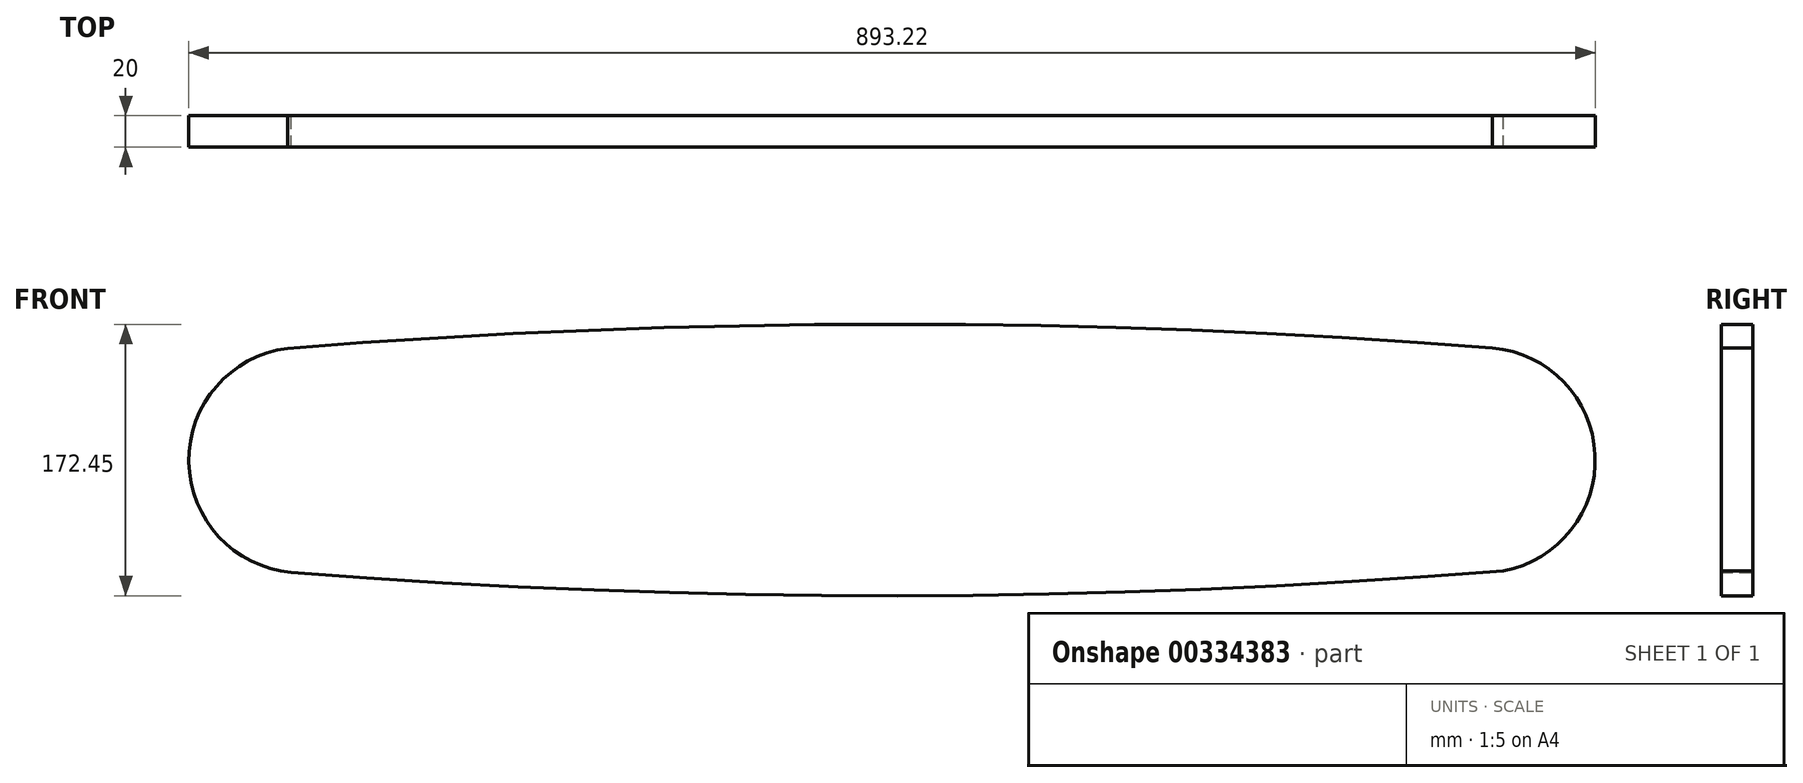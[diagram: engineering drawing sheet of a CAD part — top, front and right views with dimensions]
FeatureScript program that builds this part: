
annotation { "Feature Type Name" : "Feature", "Feature Type Description" : "" }
export const myFeature = defineFeature(function(context is Context, id is Id, definition is map)
    precondition{}
    {
        {
            var Q0;
            Q0=qCreatedBy(makeId("Front.planeOp"),FACE);
            var sketch = newSketch(context, id + "F0", { "sketchPlane" : qUnion([Q0])});
            skCircle(sketch, "E0", {"center": v(-63.48, 0) * mm, "radius": 71.61 * mm});
            skCircle(sketch, "E1", {"center": v(686.52, 0) * mm, "radius": 71.61 * mm});
            skLineSegment(sketch, "E2", {"start": v(686.52, 0) * mm, "end": v(-63.48, 0) * mm});
            skArc(sketch, "E3", {"start": v(-70.15, -71.3) * mm, "mid": v(314.9, -86.13) * mm, "end": v(699.91, -70.35) * mm});
            skArc(sketch, "E4", {"start": v(693, 71.32) * mm, "mid": v(310.28, 86.3) * mm, "end": v(-72.44, 71.05) * mm});
            skSolve(sketch);
        }
        {
            var Q0;
            {var subQ1=sQuery(id+"F0.wireOp",EDGE,"E0");var subQ4=sQuery(id+"F0.wireOp",EDGE,"E4");var subQ5=makeQuery(id+"F0.imprint","INTERSECT",VERTEX,{"disambiguationData":[OD(1.0)],"derivedFrom":[subQ1,subQ4]});Q0=makeQuery(id+"F0.imprint","IMPRINT",FACE,{"disambiguationData":[TD([[makeQuery(id+"F0.imprint","IMPRINT",EDGE,{"disambiguationData":[TD([[subQ5,1.0]])],"derivedFrom":subQ1}),1.0]])]});}
            var Q1;
            {var subQ0=sQuery(id+"F0.wireOp",EDGE,"E4");var subQ1=sQuery(id+"F0.wireOp",EDGE,"E0");var subQ2=makeQuery(id+"F0.imprint","INTERSECT",VERTEX,{"disambiguationData":[OD(1.0)],"derivedFrom":[subQ1,subQ0]});Q1=makeQuery(id+"F0.imprint","IMPRINT",FACE,{"disambiguationData":[TD([[makeQuery(id+"F0.imprint","IMPRINT",EDGE,{"disambiguationData":[TD([[subQ2,1.0]])],"derivedFrom":subQ1}),-1.0]])]});}
            var Q2;
            {var subQ0=sQuery(id+"F0.wireOp",EDGE,"E2");var subQ1=sQuery(id+"F0.wireOp",EDGE,"E0");var subQ2=makeQuery(id+"F0.imprint","INTERSECT",VERTEX,{"derivedFrom":[subQ1,subQ0]});Q2=makeQuery(id+"F0.imprint","IMPRINT",FACE,{"disambiguationData":[TD([[makeQuery(id+"F0.imprint","IMPRINT",EDGE,{"disambiguationData":[TD([[subQ2,1.0]])],"derivedFrom":subQ1}),-1.0]])]});}
            var Q3;
            {var subQ1=sQuery(id+"F0.wireOp",EDGE,"E1");var subQ4=sQuery(id+"F0.wireOp",EDGE,"E4");var subQ7=makeQuery(id+"F0.imprint","INTERSECT",VERTEX,{"disambiguationData":[OD(1.0)],"derivedFrom":[subQ1,subQ4]});Q3=makeQuery(id+"F0.imprint","IMPRINT",FACE,{"disambiguationData":[TD([[makeQuery(id+"F0.imprint","IMPRINT",EDGE,{"disambiguationData":[TD([[subQ7,-1.0]])],"derivedFrom":subQ1}),1.0]])]});}
            extrude(context, id + "F1", {"entities" : qUnion([Q0, Q1, Q2, Q3]), "depth" : 20 * mm});
        }
    });
